# Revit family: STL21151_27_30
name_source: partatom
category: Luminárias
units: mm (PartAtom-declared; Revit-internal decimal feet)

## family parameters
Com base no plano de trabalho = Não
Compartilhado = Não
Corte com vazios quando carregada = Não
Cota do conector redondo = Utilizar diâmetro
Fonte luminosa = Sim
Manter orientação da anotação = Não
Ponto de cálculo do ambiente = Não
Sempre na vertical = Sim
Tipo de parte = Normal

## types (2) — shared parameters
Altura = 0.05 m
Cromado = Cromado
Dimerização = 20-100%
Diâmetro = 0.02 m
Estrutura = Al - Branco
Fabricante = Stella
Filtro de cor = 16777215
Grau de proteção (IP) = IP20
IRC (Índice de reprodução de cores) = >80
Modelo = Bipino G9 Dimerizável
Potência = 2 W
Tensão Elétrica = 127V
Troca de temperatura da cor de lâmpada com esmaecimento = <Nenhum>
URL = https://stella.com.br
Vidro = Vidro
Ângulo de Abertura = 120°
Ângulo de inclinação = 90.00°
zero-valued in all types: Elevação padrão

## per-type parameters (varying)
| type | Arquivo de rede fotométrica | Fluxo Luminoso | Luminoso | Referência | Temperatura da cor (K) |
| STL21151/27 - 127V- 2700K - 170lm - 120° | STELLA - STL21151-27 - BIPINO G9 2W.ies | 170 lm | Luminoso - 2700K | STL21151/27 - 127V | 2700 K |
| STL21151/30 - 127V - 3000K - 180lm - 120° | STELLA - STL21151-30 - BIPINO G9 2W.ies | 180 lm | Luminoso - 3000K | STL21151/30 - 127V | 3000 K |
